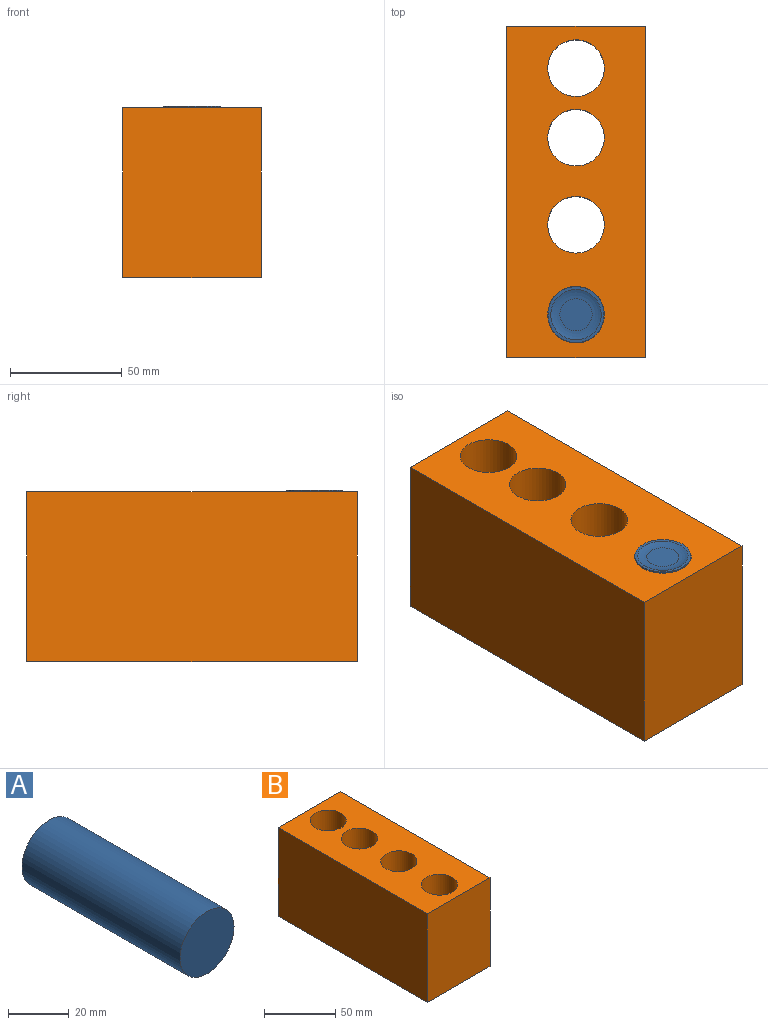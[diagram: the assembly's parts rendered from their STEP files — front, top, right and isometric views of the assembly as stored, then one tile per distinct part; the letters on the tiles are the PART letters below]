
ASSEMBLY  parts=2 mates=1
PART A: 5 faces, bbox 25.1x73.7x25.1 mm
  f0: cylinder r=12.57mm len=73.66mm, axis (0,1,0), area 5819mm2, adj f1,f2
  f1: plane 25.15x25.15mm, normal (0,-1,0), area 496.6mm2, adj f0
  f2: plane 25.15x25.15mm, normal (0,1,0), area 95.3mm2, adj f0,f4
  f3: plane 14.43x14.43mm, normal (0,1,0), area 163.6mm2, adj f4
  f4: torus R=7.22mm, axis (0,1,0), area 243.8mm2, adj f2,f3
PART B: 10 faces, bbox 62.1x148.4x76.2 mm
  f0: plane 76.2x62.11mm, normal (0,-1,0), area 4733.1mm2, adj f1,f7,f8,f9
  f1: plane 148.38x76.2mm, normal (1,0,0), area 11306.6mm2, adj f0,f2,f8,f9
  f2: plane 76.2x62.11mm, normal (0,1,0), area 4733.1mm2, adj f1,f7,f8,f9
  f3: cylinder r=12.7mm len=76.2mm, axis (0,0,-1), area 6080.5mm2, adj f8,f9
  f4: cylinder r=12.7mm len=76.2mm, axis (0,0,-1), area 6080.5mm2, adj f8,f9
  f5: cylinder r=12.7mm len=76.2mm, axis (0,0,-1), area 6080.5mm2, adj f8,f9
  f6: cylinder r=12.7mm len=76.2mm, axis (0,0,-1), area 6080.5mm2, adj f8,f9
  f7: plane 148.38x76.2mm, normal (-1,0,0), area 11306.6mm2, adj f0,f2,f8,f9
  f8: plane 148.38x62.11mm, normal (0,0,1), area 7189.7mm2, adj f0,f1,f2,f3,f4,f5,f6,f7
  f9: plane 148.38x62.11mm, normal (0,0,-1), area 7189.7mm2, adj f0,f1,f2,f3,f4,f5,f6,f7
PLACE A rot(axis=(1,0,0),90deg) t=(1.1,-97.49,24.71)mm
PLACE B t=(1.1,-42.42,-1.24)mm
MATE cylindrical A.f0 <-> B.f6  axis (0,0,1) through (1.1,-97.49,-12.12)mm
